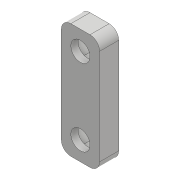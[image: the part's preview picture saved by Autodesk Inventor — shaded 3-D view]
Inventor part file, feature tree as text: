
AUTODESK INVENTOR PART (.ipt)
format: ipt  version: 2017 (Build 210142000, 142)  size: 128,000 bytes
history: native  units: mm
features: sketch x3, extrude x2, projected_geometry x2, fillet x1, hole x1
ambient origin geometry x8: Origin, YZ Plane, XZ Plane, XY Plane, X Axis, Y Axis, Z Axis, Center Point
bodies: Solid1 (feature_tree)
feature tree (9):
  extrude  "Extrusion1"  Depth=24.0mm
  extrude  "Extrusion2"  TaperAngle=0.0deg  [1 undecoded]
  fillet  "Fillet1"  Radius=8.0mm
  hole  "Hole1"  [1 undecoded]
  sketch  "Sketch1"  dims[d0=8.0mm d1=24.0mm]
  sketch  "Sketch2"  dims[d2=4.0mm d3=0.0mm d4=0.0mm d5=8.0mm]
  sketch  "Sketch3"  dims[d6=5.5mm d7=2.5mm d8=0.0mm d9=2.0mm d10=4.0mm d11=6.0mm d12=4.0mm d13=2.0mm d14=90.0deg d15=8.0mm d16=20.594885mm]
  projected_geometry  "Projected Loop1"
  projected_geometry  "Projected Loop2"
note: 2 required parameter values undecoded (feature->parameter linkage not recoverable at this tier; creation-order binding heuristic only, values carry confidence <= 0.55)
